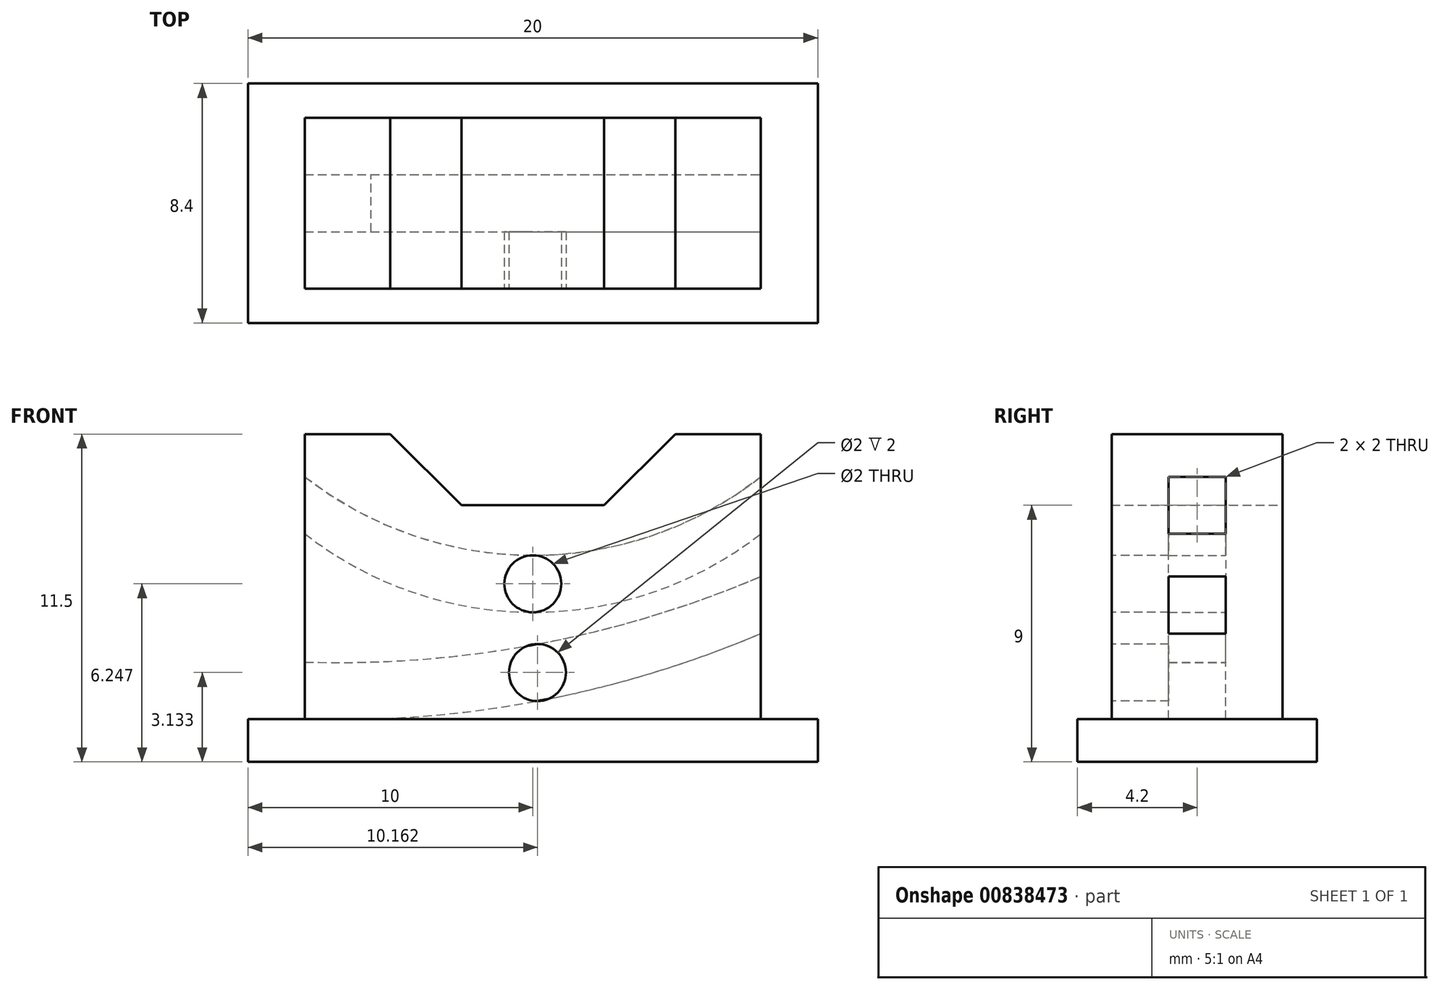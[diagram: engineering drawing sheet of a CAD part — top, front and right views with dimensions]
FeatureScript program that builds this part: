
annotation { "Feature Type Name" : "Feature", "Feature Type Description" : "" }
export const myFeature = defineFeature(function(context is Context, id is Id, definition is map)
    precondition{}
    {
        {
            var Q0;
            Q0=qCreatedBy(makeId("Top.planeOp"),FACE);
            var sketch = newSketch(context, id + "F0", { "sketchPlane" : qUnion([Q0])});
            skLineSegment(sketch, "E0.bottom", {"start": v(-10, 4.2) * mm, "end": v(10, 4.2) * mm});
            skLineSegment(sketch, "E0.top", {"start": v(-10, -4.2) * mm, "end": v(10, -4.2) * mm});
            skLineSegment(sketch, "E0.left", {"start": v(-10, 4.2) * mm, "end": v(-10, -4.2) * mm});
            skLineSegment(sketch, "E0.right", {"start": v(10, 4.2) * mm, "end": v(10, -4.2) * mm});
            skLineSegment(sketch, "E1", {"start": v(0, 4.2) * mm, "end": v(0, -4.2) * mm});
            skSolve(sketch);
        }
        {
            var Q0;
            Q0=makeQuery(id+"F0.imprint","IMPRINT",FACE,{"disambiguationData":[TD([[makeQuery(id+"F0.imprint","IMPRINT",EDGE,{"derivedFrom":sQuery(id+"F0.wireOp",EDGE,"E0.bottom")}),-1.0]])]});
            extrude(context, id + "F1", {"entities" : qUnion([Q0]), "oppositeDirection" : true, "depth" : 1.5 * mm, "offsetDistance" : 25 * mm});
        }
        {
            var Q0;
            Q0=qCreatedBy(makeId("Front.planeOp"),FACE);
            var sketch = newSketch(context, id + "F2", { "sketchPlane" : qUnion([Q0])});
            skLineSegment(sketch, "E2.bottom", {"start": v(-8, 0) * mm, "end": v(8, 0) * mm});
            skLineSegment(sketch, "E2.top", {"start": v(-8, 10) * mm, "end": v(8, 10) * mm});
            skLineSegment(sketch, "E2.left", {"start": v(-8, 0) * mm, "end": v(-8, 10) * mm});
            skLineSegment(sketch, "E2.right", {"start": v(8, 0) * mm, "end": v(8, 10) * mm});
            skArc(sketch, "E3", {"start": v(-8, 0) * mm, "mid": v(0.16, 0.63) * mm, "end": v(8, 3) * mm});
            skArc(sketch, "E4", {"start": v(-8, 2) * mm, "mid": v(0.16, 2.63) * mm, "end": v(8, 5) * mm});
            skArc(sketch, "E5", {"start": v(-8, 6.5) * mm, "mid": v(0, 3.75) * mm, "end": v(8, 6.5) * mm});
            skArc(sketch, "E6", {"start": v(-8, 8.5) * mm, "mid": v(0, 5.75) * mm, "end": v(8, 8.5) * mm});
            skLineSegment(sketch, "E7", {"start": v(-5, 10) * mm, "end": v(-2.5, 7.5) * mm});
            skLineSegment(sketch, "E8", {"start": v(-2.5, 7.5) * mm, "end": v(2.5, 7.5) * mm});
            skLineSegment(sketch, "E9", {"start": v(2.5, 7.5) * mm, "end": v(5, 10) * mm});
            skPoint(sketch, "E10", {"position": v(0, 7.5) * mm});
            skSolve(sketch);
        }
        {
            var Q0;
            {var subQ0=sQuery(id+"F2.wireOp",EDGE,"E5");Q0=makeQuery(id+"F2.imprint","IMPRINT",FACE,{"disambiguationData":[TD([[makeQuery(id+"F2.imprint","IMPRINT",EDGE,{"derivedFrom":subQ0}),1.0]])]});}
            var Q1;
            {var subQ0=sQuery(id+"F2.wireOp",EDGE,"E2.top");Q1=makeQuery(id+"F2.imprint","IMPRINT",FACE,{"disambiguationData":[TD([[makeQuery(id+"F2.imprint","IMPRINT",EDGE,{"derivedFrom":subQ0}),-1.0]])]});}
            var Q2;
            {var subQ0=sQuery(id+"F2.wireOp",EDGE,"E4");Q2=makeQuery(id+"F2.imprint","IMPRINT",FACE,{"disambiguationData":[TD([[makeQuery(id+"F2.imprint","IMPRINT",EDGE,{"derivedFrom":subQ0}),1.0]])]});}
            var Q3;
            {var subQ5=sQuery(id+"F2.wireOp",EDGE,"E4");Q3=makeQuery(id+"F2.imprint","IMPRINT",FACE,{"disambiguationData":[TD([[makeQuery(id+"F2.imprint","IMPRINT",EDGE,{"derivedFrom":subQ5}),-1.0]])]});}
            var Q4;
            {var subQ0=sQuery(id+"F2.wireOp",EDGE,"E2.right");var subQ1=sQuery(id+"F2.wireOp",EDGE,"E2.bottom");var subQ2=makeQuery(id+"F2.imprint","INTERSECT",VERTEX,{"derivedFrom":[subQ1,subQ0]});Q4=makeQuery(id+"F2.imprint","IMPRINT",FACE,{"disambiguationData":[TD([[makeQuery(id+"F2.imprint","IMPRINT",EDGE,{"disambiguationData":[TD([[subQ2,1.0]])],"derivedFrom":subQ1}),1.0]])]});}
            extrude(context, id + "F3", {"entities" : qUnion([Q0, Q1, Q2, Q3, Q4]), "operationType" : NewBodyOperationType.ADD, "depth" : 6 * mm, "offsetDistance" : 25 * mm, "symmetric" : true});
        }
        {
            var Q0;
            {var subQ0=sQuery(id+"F2.wireOp",EDGE,"E5");Q0=makeQuery(id+"F2.imprint","IMPRINT",FACE,{"disambiguationData":[TD([[makeQuery(id+"F2.imprint","IMPRINT",EDGE,{"derivedFrom":subQ0}),1.0]])]});}
            var Q1;
            {var subQ5=sQuery(id+"F2.wireOp",EDGE,"E4");Q1=makeQuery(id+"F2.imprint","IMPRINT",FACE,{"disambiguationData":[TD([[makeQuery(id+"F2.imprint","IMPRINT",EDGE,{"derivedFrom":subQ5}),-1.0]])]});}
            extrude(context, id + "F4", {"entities" : qUnion([Q0, Q1]), "operationType" : NewBodyOperationType.REMOVE, "depth" : 2 * mm, "offsetDistance" : 25 * mm, "symmetric" : true});
        }
        {
            var Q0;
            Q0=makeQuery(id+"F3.opExtrude","CAP_FACE",FACE,{"disambiguationData":[OSD([sQuery(id+"F2.wireOp",EDGE,"E2.bottom"),sQuery(id+"F2.wireOp",EDGE,"E2.top"),sQuery(id+"F2.wireOp",EDGE,"E2.left"),sQuery(id+"F2.wireOp",EDGE,"E2.right")])],"isStart":false});
            var sketch = newSketch(context, id + "F5", { "sketchPlane" : qUnion([Q0])});
            skPoint(sketch, "E11.0", {"position": v(0, 3.75) * mm});
            skPoint(sketch, "E11.1", {"position": v(0, 5.75) * mm});
            skPoint(sketch, "E11.2", {"position": v(0.16, 0.63) * mm});
            skPoint(sketch, "E11.3", {"position": v(0.16, 2.63) * mm});
            skCircle(sketch, "E12", {"center": v(0, 4.75) * mm, "radius": 1 * mm});
            skCircle(sketch, "E13", {"center": v(0.16, 1.63) * mm, "radius": 1 * mm});
            skSolve(sketch);
        }
        {
            var Q0;
            Q0=makeQuery(id+"F5.imprint","IMPRINT",FACE,{"disambiguationData":[TD([[makeQuery(id+"F5.imprint","IMPRINT",EDGE,{"derivedFrom":sQuery(id+"F5.wireOp",EDGE,"E12")}),1.0]])]});
            var Q1;
            Q1=makeQuery(id+"F5.imprint","IMPRINT",FACE,{"disambiguationData":[TD([[makeQuery(id+"F5.imprint","IMPRINT",EDGE,{"derivedFrom":sQuery(id+"F5.wireOp",EDGE,"E13")}),1.0]])]});
            extrude(context, id + "F6", {"entities" : qUnion([Q0, Q1]), "operationType" : NewBodyOperationType.REMOVE, "oppositeDirection" : true, "depth" : 2 * mm, "offsetDistance" : 25 * mm});
        }
    });
